# Revit family: ME_Оборудование [узел угловой для нижнего подключения радиатора угловой VT.345.NA]1 - VALTEC
name_source: partatom
category: Оборудование
revit_build: Autodesk Revit 2018 (Build: 20180423_1000(x64)
units: mm (PartAtom-declared; Revit-internal decimal feet)

## family parameters
Всегда вертикально = Да
Классификация = Нет
На основе рабочей плоскости = Нет
Общий = Нет
При загрузке вырезать с полостями = Нет
Размер круглого соединителя = Использовать диаметр
Тип детали = Вставляется
Точка расчета площади = Нет

## types (1)
- VT.345.NA
    ADSK_URL документации изделия = https://valtec.ru
    ADSK_URL страницы изделия = https://valtec.ru
    ADSK_Материал = Сталь, нержавеющая - VALTEC
    URL = https://valtec.ru
    Изготовитель = VALTEC
    Материал доп.1 = Черный - VALTEC
    Материал доп.2 = Латунь - VALTEC
    Таблица 1 = ME_Оборудование [узел угловой для нижнего подключения радиатора угловой VT.345.NA] - VALTEC - Таблица 1
    Таблица 2 = ME_Оборудование [узел угловой для нижнего подключения радиатора угловой VT.345.NA] - VALTEC - Таблица 2
